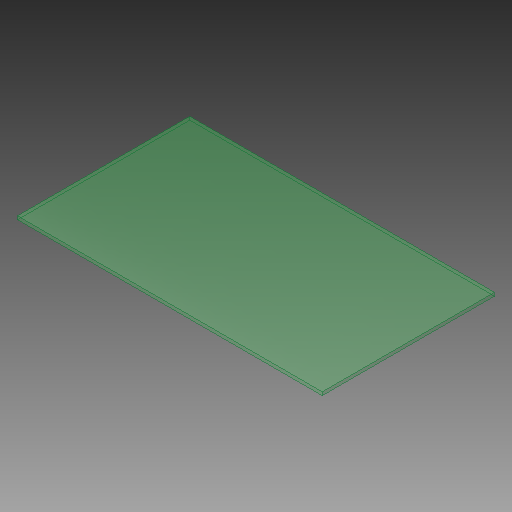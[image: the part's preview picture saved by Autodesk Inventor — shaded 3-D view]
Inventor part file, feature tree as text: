
AUTODESK INVENTOR PART (.ipt)
format: ipt  version: 2018.1 (Build 221171000, 171)  size: 93,184 bytes
history: native  units: mm
features: extrude x1, sketch x1
ambient origin geometry x8: Origin, YZ Plane, XZ Plane, XY Plane, X Axis, Y Axis, Z Axis, Center Point
bodies: Solid1 (feature_tree)
feature tree (2):
  extrude  "Extrusion1"  Depth=260.0mm
  sketch  "Sketch1"  dims[d0=460.0mm d1=260.0mm d2=5.0mm d3=0.0mm]
